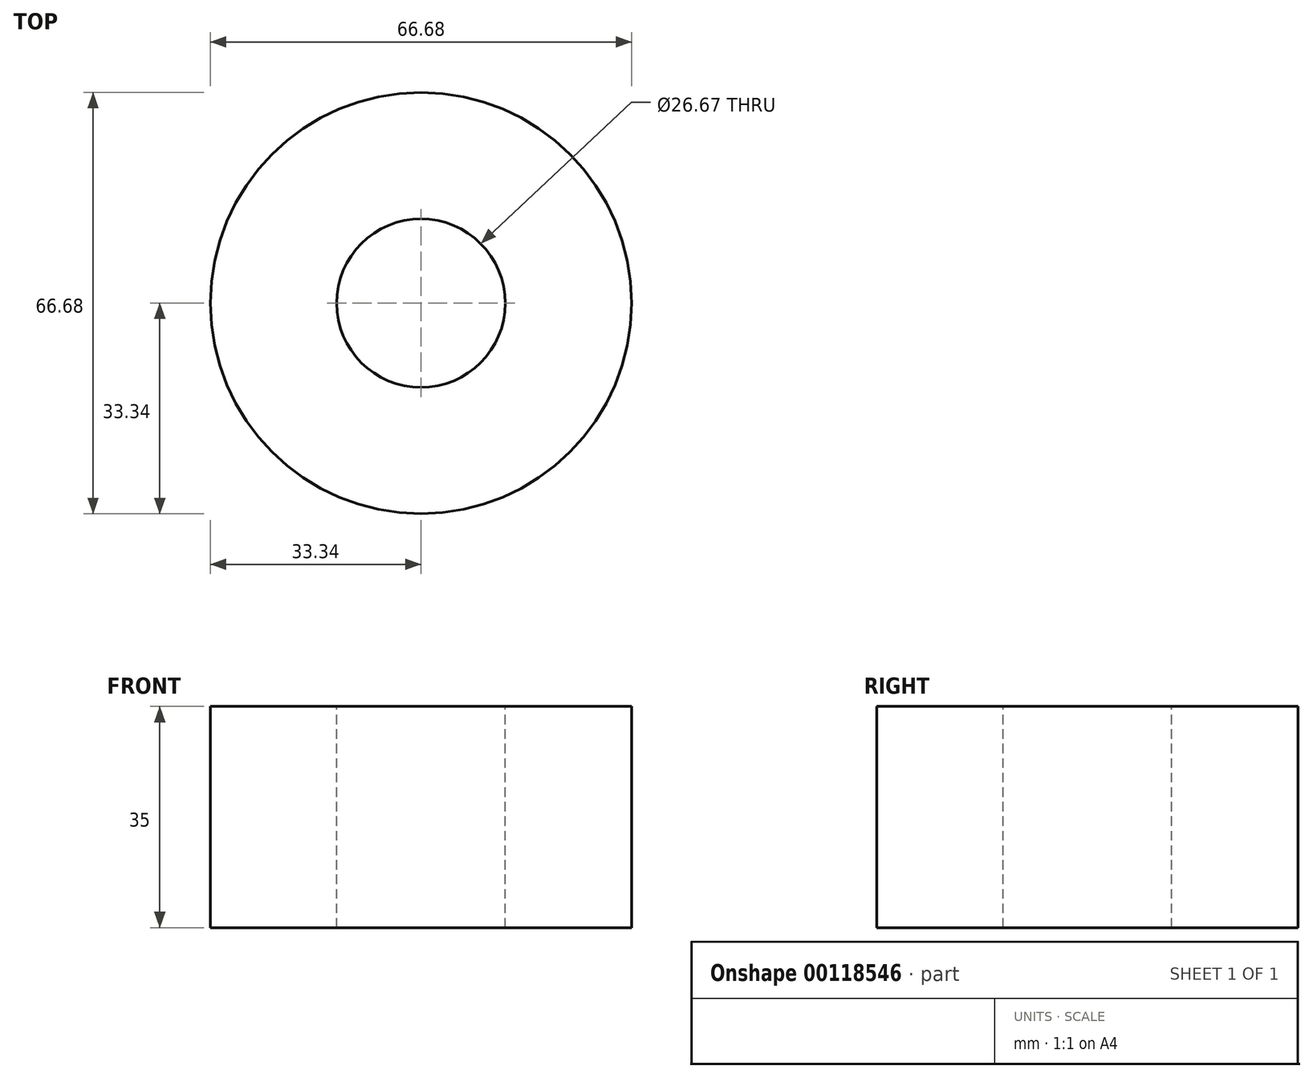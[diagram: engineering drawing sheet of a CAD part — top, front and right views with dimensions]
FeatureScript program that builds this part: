
annotation { "Feature Type Name" : "Feature", "Feature Type Description" : "" }
export const myFeature = defineFeature(function(context is Context, id is Id, definition is map)
    precondition{}
    {
        {
            var Q0;
            Q0=qCreatedBy(makeId("Top.planeOp"),FACE);
            var sketch = newSketch(context, id + "F0", { "sketchPlane" : qUnion([Q0])});
            skCircle(sketch, "E0", {"center": v(0, 0) * mm, "radius": 13.33 * mm, "construction": true});
            skCircle(sketch, "E1", {"center": v(0, 0) * mm, "radius": 23.33 * mm, "construction": true});
            skCircle(sketch, "E2", {"center": v(0, 0) * mm, "radius": 33.34 * mm});
            skSolve(sketch);
        }
        {
            var Q0;
            Q0=makeQuery(id+"F0.imprint","IMPRINT",FACE,{"disambiguationData":[TD([[makeQuery(id+"F0.imprint","IMPRINT",EDGE,{"derivedFrom":sQuery(id+"F0.wireOp",EDGE,"E2")}),1.0]])]});
            extrude(context, id + "F1", {"entities" : qUnion([Q0]), "depth" : 35 * mm, "offsetDistance" : 25.4 * mm});
        }
        {
            var Q0;
            Q0=makeQuery(id+"F1.opExtrude","CAP_FACE",FACE,{"disambiguationData":[OSD([sQuery(id+"F0.wireOp",EDGE,"E2")])],"isStart":false});
            var sketch = newSketch(context, id + "F2", { "sketchPlane" : qUnion([Q0])});
            skCircle(sketch, "E3", {"center": v(0, 0) * mm, "radius": 13.34 * mm});
            skSolve(sketch);
        }
        {
            var Q0;
            Q0=makeQuery(id+"F2.imprint","IMPRINT",FACE,{"disambiguationData":[TD([[makeQuery(id+"F2.imprint","IMPRINT",EDGE,{"derivedFrom":sQuery(id+"F2.wireOp",EDGE,"E3")}),1.0]])]});
            extrude(context, id + "F3", {"entities" : qUnion([Q0]), "operationType" : NewBodyOperationType.REMOVE, "endBound" : BoundingType.UP_TO_NEXT, "oppositeDirection" : true, "depth" : 25.4 * mm});
        }
    });
